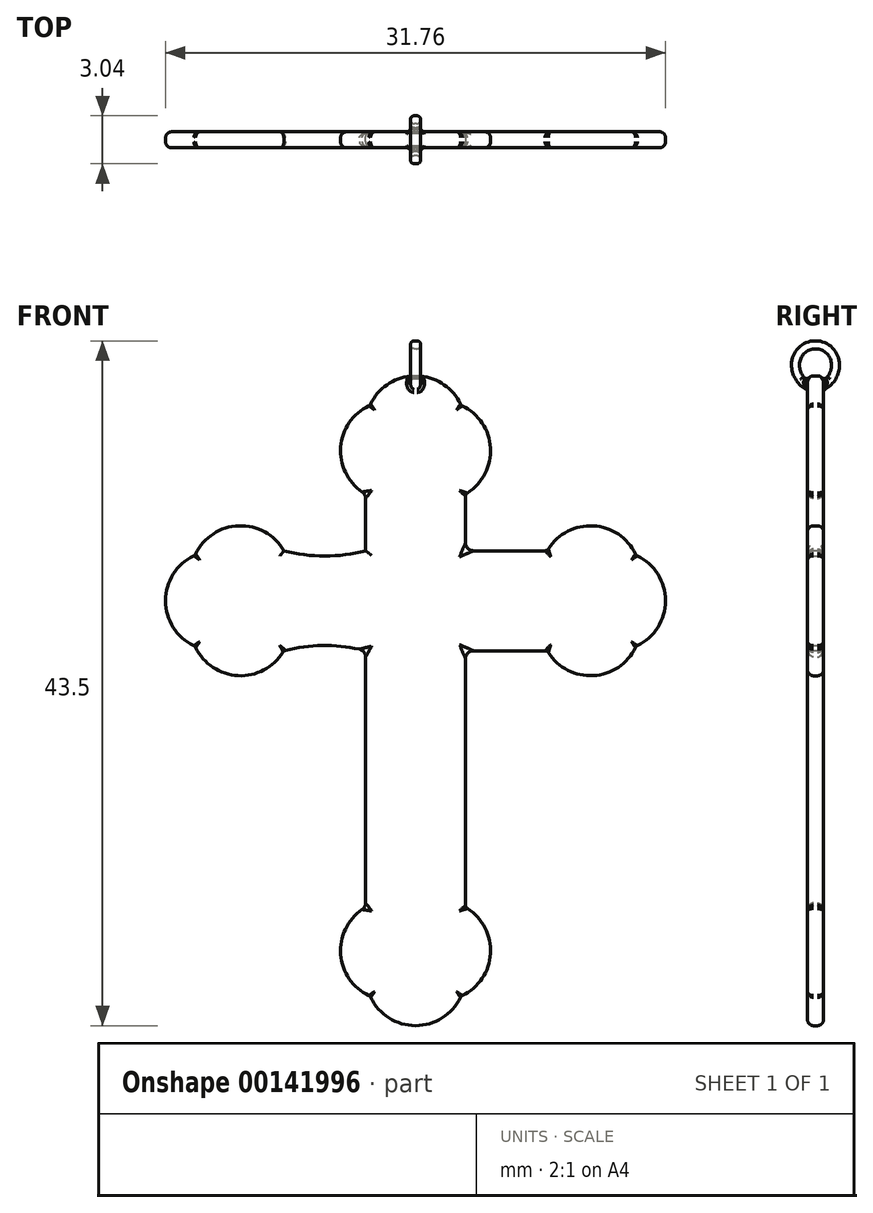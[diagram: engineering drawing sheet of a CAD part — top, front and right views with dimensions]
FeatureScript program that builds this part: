
annotation { "Feature Type Name" : "Feature", "Feature Type Description" : "" }
export const myFeature = defineFeature(function(context is Context, id is Id, definition is map)
    precondition{}
    {
        {
            var Q0;
            Q0=qCreatedBy(makeId("Front.planeOp"),FACE);
            var sketch = newSketch(context, id + "F0", { "sketchPlane" : qUnion([Q0])});
            skLineSegment(sketch, "E0", {"start": v(-3.17, 3.18) * mm, "end": v(-3.17, 6.78) * mm});
            skLineSegment(sketch, "E1", {"start": v(-3.17, 11.11) * mm, "end": v(0, 11.11) * mm, "construction": true});
            skLineSegment(sketch, "E2", {"start": v(0, 11.11) * mm, "end": v(0, -23.81) * mm, "construction": true});
            skLineSegment(sketch, "E3", {"start": v(0, -23.81) * mm, "end": v(-3.17, -23.81) * mm, "construction": true});
            skLineSegment(sketch, "E4", {"start": v(-3.17, -19.48) * mm, "end": v(-3.17, -3.17) * mm});
            skLineSegment(sketch, "E5", {"start": v(-3.17, -3.17) * mm, "end": v(-8.36, -3.17) * mm, "construction": true});
            skLineSegment(sketch, "E6", {"start": v(-12.7, -3.18) * mm, "end": v(-12.7, 0) * mm, "construction": true});
            skLineSegment(sketch, "E7", {"start": v(-8.36, 3.18) * mm, "end": v(-3.17, 3.18) * mm, "construction": true});
            skLineSegment(sketch, "E8", {"start": v(0, 0) * mm, "end": v(-12.7, 0) * mm, "construction": true});
            skLineSegment(sketch, "E9.MirrorCS", {"start": v(3.17, 3.18) * mm, "end": v(3.17, 6.78) * mm});
            skLineSegment(sketch, "E10.MirrorCS", {"start": v(3.17, -19.48) * mm, "end": v(3.17, -3.17) * mm});
            skLineSegment(sketch, "E11.MirrorCS", {"start": v(0, 0) * mm, "end": v(12.7, 0) * mm, "construction": true});
            skLineSegment(sketch, "E12.MirrorCS", {"start": v(12.7, -3.18) * mm, "end": v(12.7, 0) * mm, "construction": true});
            skLineSegment(sketch, "E13.MirrorCS", {"start": v(8.36, 3.18) * mm, "end": v(3.17, 3.18) * mm});
            skLineSegment(sketch, "E14.MirrorCS", {"start": v(3.17, -3.17) * mm, "end": v(8.36, -3.17) * mm});
            skArc(sketch, "E15", {"start": v(2.9, 12.42) * mm, "mid": v(0, 14.29) * mm, "end": v(-2.9, 12.42) * mm});
            skArc(sketch, "E16", {"start": v(-2.9, 12.42) * mm, "mid": v(-4.76, 9.68) * mm, "end": v(-3.17, 6.78) * mm});
            skLineSegment(sketch, "E17", {"start": v(-3.17, 11.11) * mm, "end": v(-1.59, 9.53) * mm, "construction": true});
            skLineSegment(sketch, "E18", {"start": v(0, 11.11) * mm, "end": v(-1.59, 9.53) * mm, "construction": true});
            skArc(sketch, "E19.MirrorCS", {"start": v(2.9, 12.42) * mm, "mid": v(4.76, 9.68) * mm, "end": v(3.17, 6.78) * mm});
            skPoint(sketch, "E20.orphan", {"position": v(3.17, 11.11) * mm});
            skArc(sketch, "E21", {"start": v(-14, 2.9) * mm, "mid": v(-15.88, 0) * mm, "end": v(-14, -2.9) * mm});
            skLineSegment(sketch, "E22", {"start": v(-12.7, -3.18) * mm, "end": v(-11.11, -1.59) * mm, "construction": true});
            skLineSegment(sketch, "E23", {"start": v(-11.11, -1.59) * mm, "end": v(-12.7, 0) * mm, "construction": true});
            skArc(sketch, "E24", {"start": v(-14, -2.9) * mm, "mid": v(-11.27, -4.76) * mm, "end": v(-8.36, -3.17) * mm});
            skArc(sketch, "E25.MirrorCS", {"start": v(-14, 2.9) * mm, "mid": v(-11.27, 4.76) * mm, "end": v(-8.36, 3.17) * mm});
            skPoint(sketch, "E26.orphan", {"position": v(-12.7, 3.17) * mm});
            skArc(sketch, "E27.MirrorCS", {"start": v(14, 2.9) * mm, "mid": v(11.27, 4.76) * mm, "end": v(8.36, 3.17) * mm});
            skArc(sketch, "E28.MirrorCS", {"start": v(14, 2.9) * mm, "mid": v(15.88, 0) * mm, "end": v(14, -2.9) * mm});
            skArc(sketch, "E29.MirrorCS", {"start": v(14, -2.9) * mm, "mid": v(11.27, -4.76) * mm, "end": v(8.36, -3.17) * mm});
            skPoint(sketch, "E30.orphan", {"position": v(12.7, 3.18) * mm});
            skArc(sketch, "E31", {"start": v(-2.9, -25.12) * mm, "mid": v(0, -26.99) * mm, "end": v(2.9, -25.12) * mm});
            skLineSegment(sketch, "E32", {"start": v(-3.17, -23.81) * mm, "end": v(-1.59, -22.23) * mm, "construction": true});
            skLineSegment(sketch, "E33", {"start": v(-1.59, -22.23) * mm, "end": v(0, -23.81) * mm, "construction": true});
            skArc(sketch, "E34", {"start": v(-3.17, -19.48) * mm, "mid": v(-4.76, -22.38) * mm, "end": v(-2.9, -25.12) * mm});
            skArc(sketch, "E35.MirrorCS", {"start": v(3.17, -19.48) * mm, "mid": v(4.76, -22.38) * mm, "end": v(2.9, -25.12) * mm});
            skArc(sketch, "E36", {"start": v(-8.36, 3.18) * mm, "mid": v(-5.77, 2.84) * mm, "end": v(-3.17, 3.18) * mm});
            skArc(sketch, "E37.MirrorCS", {"start": v(-8.36, -3.18) * mm, "mid": v(-5.77, -2.84) * mm, "end": v(-3.17, -3.18) * mm});
            skLineSegment(sketch, "E38.MirrorCS", {"start": v(-3.17, 3.17) * mm, "end": v(-8.36, 3.17) * mm});
            skSolve(sketch);
        }
        {
            var Q0;
            Q0=makeQuery(id+"F0.imprint","IMPRINT",FACE,{"disambiguationData":[TD([[makeQuery(id+"F0.imprint","IMPRINT",EDGE,{"derivedFrom":sQuery(id+"F0.wireOp",EDGE,"E0")}),-1.0]])]});
            extrude(context, id + "F1", {"entities" : qUnion([Q0]), "endBound" : BoundingType.SYMMETRIC, "depth" : 1.02 * mm});
        }
        {
            var Q0;
            Q0=makeQuery(id+"F1.opExtrude","CAP_FACE",FACE,{"disambiguationData":[OSD([sQuery(id+"F0.wireOp",EDGE,"E0"),sQuery(id+"F0.wireOp",EDGE,"E4"),sQuery(id+"F0.wireOp",EDGE,"E5"),sQuery(id+"F0.wireOp",EDGE,"E7"),sQuery(id+"F0.wireOp",EDGE,"E9.MirrorCS"),sQuery(id+"F0.wireOp",EDGE,"E10.MirrorCS"),sQuery(id+"F0.wireOp",EDGE,"E13.MirrorCS"),sQuery(id+"F0.wireOp",EDGE,"E14.MirrorCS"),sQuery(id+"F0.wireOp",EDGE,"E15"),sQuery(id+"F0.wireOp",EDGE,"E16"),sQuery(id+"F0.wireOp",EDGE,"E19.MirrorCS"),sQuery(id+"F0.wireOp",EDGE,"E21"),sQuery(id+"F0.wireOp",EDGE,"E24"),sQuery(id+"F0.wireOp",EDGE,"E25.MirrorCS"),sQuery(id+"F0.wireOp",EDGE,"E27.MirrorCS"),sQuery(id+"F0.wireOp",EDGE,"E28.MirrorCS"),sQuery(id+"F0.wireOp",EDGE,"E29.MirrorCS"),sQuery(id+"F0.wireOp",EDGE,"E31"),sQuery(id+"F0.wireOp",EDGE,"E34"),sQuery(id+"F0.wireOp",EDGE,"E35.MirrorCS")])],"isStart":false});
            fillet(context, id + "F2", {"entities" : qUnion([Q0]), "radius" : 0.38 * mm, "tangentPropagation" : true, "allowEdgeOverflow" : false});
        }
        {
            var Q0;
            Q0=makeQuery(id+"F1.opExtrude","CAP_FACE",FACE,{"disambiguationData":[OSD([sQuery(id+"F0.wireOp",EDGE,"E0"),sQuery(id+"F0.wireOp",EDGE,"E4"),sQuery(id+"F0.wireOp",EDGE,"E5"),sQuery(id+"F0.wireOp",EDGE,"E7"),sQuery(id+"F0.wireOp",EDGE,"E9.MirrorCS"),sQuery(id+"F0.wireOp",EDGE,"E10.MirrorCS"),sQuery(id+"F0.wireOp",EDGE,"E13.MirrorCS"),sQuery(id+"F0.wireOp",EDGE,"E14.MirrorCS"),sQuery(id+"F0.wireOp",EDGE,"E15"),sQuery(id+"F0.wireOp",EDGE,"E16"),sQuery(id+"F0.wireOp",EDGE,"E19.MirrorCS"),sQuery(id+"F0.wireOp",EDGE,"E21"),sQuery(id+"F0.wireOp",EDGE,"E24"),sQuery(id+"F0.wireOp",EDGE,"E25.MirrorCS"),sQuery(id+"F0.wireOp",EDGE,"E27.MirrorCS"),sQuery(id+"F0.wireOp",EDGE,"E28.MirrorCS"),sQuery(id+"F0.wireOp",EDGE,"E29.MirrorCS"),sQuery(id+"F0.wireOp",EDGE,"E31"),sQuery(id+"F0.wireOp",EDGE,"E34"),sQuery(id+"F0.wireOp",EDGE,"E35.MirrorCS")])],"isStart":true});
            fillet(context, id + "F3", {"entities" : qUnion([Q0]), "radius" : 0.38 * mm, "tangentPropagation" : true, "allowEdgeOverflow" : false});
        }
        {
            var Q0;
            Q0=qCreatedBy(makeId("Right.planeOp"),FACE);
            var sketch = newSketch(context, id + "F4", { "sketchPlane" : qUnion([Q0])});
            skLineSegment(sketch, "E39", {"start": v(0, 0) * mm, "end": v(0, 14.99) * mm, "construction": true});
            skArc(sketch, "E40", {"start": v(-1.02, 14.99) * mm, "mid": v(-0.73, 14.18) * mm, "end": v(0, 13.74) * mm});
            skLineSegment(sketch, "E41", {"start": v(0, 14.99) * mm, "end": v(0.25, 14.99) * mm, "construction": true});
            skLineSegment(sketch, "E42", {"start": v(0, 14.99) * mm, "end": v(-0.25, 14.99) * mm, "construction": true});
            skArc(sketch, "E43", {"start": v(0, 13.74) * mm, "mid": v(0.73, 14.18) * mm, "end": v(1.02, 14.99) * mm});
            skArc(sketch, "E44", {"start": v(1.02, 14.99) * mm, "mid": v(0, 16) * mm, "end": v(-1.02, 14.99) * mm});
            skArc(sketch, "E45.0", {"start": v(1.52, 14.99) * mm, "mid": v(0, 16.51) * mm, "end": v(-1.52, 14.99) * mm});
            skArc(sketch, "E46.0", {"start": v(-1.52, 14.99) * mm, "mid": v(-1.1, 13.82) * mm, "end": v(0, 13.23) * mm});
            skArc(sketch, "E47.0", {"start": v(0, 13.23) * mm, "mid": v(1.1, 13.82) * mm, "end": v(1.52, 14.99) * mm});
            skSolve(sketch);
        }
        {
            var Q0;
            Q0=qSketchRegion(id+"F4",true);
            extrude(context, id + "F5", {"entities" : qUnion([Q0]), "operationType" : NewBodyOperationType.ADD, "endBound" : BoundingType.SYMMETRIC, "depth" : 0.64 * mm});
        }
        {
            var Q0;
            Q0=makeQuery(id+"F5.opExtrude","SWEPT_FACE",FACE,{"disambiguationData":[OSD([sQuery(id+"F4.wireOp",EDGE,"E45.0")])]});
            fillet(context, id + "F6", {"entities" : qUnion([Q0]), "radius" : 0.23 * mm, "tangentPropagation" : true, "allowEdgeOverflow" : false});
        }
        {
            var Q0;
            Q0=makeQuery(id+"F6.opFillet","BLEND_EDGE",EDGE,{"blendedFrom":[makeQuery(id+"F5.opExtrude","CAP_EDGE",EDGE,{"disambiguationData":[OSD([sQuery(id+"F4.wireOp",EDGE,"E47.0")])],"isStart":false}),makeQuery(id+"F1.opExtrude","CAP_FACE",FACE,{"disambiguationData":[OSD([sQuery(id+"F0.wireOp",EDGE,"E0"),sQuery(id+"F0.wireOp",EDGE,"E4"),sQuery(id+"F0.wireOp",EDGE,"E5"),sQuery(id+"F0.wireOp",EDGE,"E7"),sQuery(id+"F0.wireOp",EDGE,"E9.MirrorCS"),sQuery(id+"F0.wireOp",EDGE,"E10.MirrorCS"),sQuery(id+"F0.wireOp",EDGE,"E13.MirrorCS"),sQuery(id+"F0.wireOp",EDGE,"E14.MirrorCS"),sQuery(id+"F0.wireOp",EDGE,"E15"),sQuery(id+"F0.wireOp",EDGE,"E16"),sQuery(id+"F0.wireOp",EDGE,"E19.MirrorCS"),sQuery(id+"F0.wireOp",EDGE,"E21"),sQuery(id+"F0.wireOp",EDGE,"E24"),sQuery(id+"F0.wireOp",EDGE,"E25.MirrorCS"),sQuery(id+"F0.wireOp",EDGE,"E27.MirrorCS"),sQuery(id+"F0.wireOp",EDGE,"E28.MirrorCS"),sQuery(id+"F0.wireOp",EDGE,"E29.MirrorCS"),sQuery(id+"F0.wireOp",EDGE,"E31"),sQuery(id+"F0.wireOp",EDGE,"E34"),sQuery(id+"F0.wireOp",EDGE,"E35.MirrorCS")])],"isStart":true})],"blendedInto":[makeQuery(id+"F1.opExtrude","CAP_FACE",FACE,{"disambiguationData":[OSD([sQuery(id+"F0.wireOp",EDGE,"E0"),sQuery(id+"F0.wireOp",EDGE,"E4"),sQuery(id+"F0.wireOp",EDGE,"E5"),sQuery(id+"F0.wireOp",EDGE,"E7"),sQuery(id+"F0.wireOp",EDGE,"E9.MirrorCS"),sQuery(id+"F0.wireOp",EDGE,"E10.MirrorCS"),sQuery(id+"F0.wireOp",EDGE,"E13.MirrorCS"),sQuery(id+"F0.wireOp",EDGE,"E14.MirrorCS"),sQuery(id+"F0.wireOp",EDGE,"E15"),sQuery(id+"F0.wireOp",EDGE,"E16"),sQuery(id+"F0.wireOp",EDGE,"E19.MirrorCS"),sQuery(id+"F0.wireOp",EDGE,"E21"),sQuery(id+"F0.wireOp",EDGE,"E24"),sQuery(id+"F0.wireOp",EDGE,"E25.MirrorCS"),sQuery(id+"F0.wireOp",EDGE,"E27.MirrorCS"),sQuery(id+"F0.wireOp",EDGE,"E28.MirrorCS"),sQuery(id+"F0.wireOp",EDGE,"E29.MirrorCS"),sQuery(id+"F0.wireOp",EDGE,"E31"),sQuery(id+"F0.wireOp",EDGE,"E34"),sQuery(id+"F0.wireOp",EDGE,"E35.MirrorCS")])],"isStart":true})]});
            fillet(context, id + "F7", {"entities" : qUnion([Q0]), "radius" : 0.25 * mm, "tangentPropagation" : true, "allowEdgeOverflow" : false});
        }
        {
            var Q0;
            Q0=makeQuery(id+"F6.opFillet","BLEND_EDGE",EDGE,{"blendedFrom":[makeQuery(id+"F5.opExtrude","CAP_EDGE",EDGE,{"disambiguationData":[OSD([sQuery(id+"F4.wireOp",EDGE,"E46.0")])],"isStart":true}),makeQuery(id+"F1.opExtrude","CAP_FACE",FACE,{"disambiguationData":[OSD([sQuery(id+"F0.wireOp",EDGE,"E0"),sQuery(id+"F0.wireOp",EDGE,"E4"),sQuery(id+"F0.wireOp",EDGE,"E5"),sQuery(id+"F0.wireOp",EDGE,"E7"),sQuery(id+"F0.wireOp",EDGE,"E9.MirrorCS"),sQuery(id+"F0.wireOp",EDGE,"E10.MirrorCS"),sQuery(id+"F0.wireOp",EDGE,"E13.MirrorCS"),sQuery(id+"F0.wireOp",EDGE,"E14.MirrorCS"),sQuery(id+"F0.wireOp",EDGE,"E15"),sQuery(id+"F0.wireOp",EDGE,"E16"),sQuery(id+"F0.wireOp",EDGE,"E19.MirrorCS"),sQuery(id+"F0.wireOp",EDGE,"E21"),sQuery(id+"F0.wireOp",EDGE,"E24"),sQuery(id+"F0.wireOp",EDGE,"E25.MirrorCS"),sQuery(id+"F0.wireOp",EDGE,"E27.MirrorCS"),sQuery(id+"F0.wireOp",EDGE,"E28.MirrorCS"),sQuery(id+"F0.wireOp",EDGE,"E29.MirrorCS"),sQuery(id+"F0.wireOp",EDGE,"E31"),sQuery(id+"F0.wireOp",EDGE,"E34"),sQuery(id+"F0.wireOp",EDGE,"E35.MirrorCS")])],"isStart":false})],"blendedInto":[makeQuery(id+"F1.opExtrude","CAP_FACE",FACE,{"disambiguationData":[OSD([sQuery(id+"F0.wireOp",EDGE,"E0"),sQuery(id+"F0.wireOp",EDGE,"E4"),sQuery(id+"F0.wireOp",EDGE,"E5"),sQuery(id+"F0.wireOp",EDGE,"E7"),sQuery(id+"F0.wireOp",EDGE,"E9.MirrorCS"),sQuery(id+"F0.wireOp",EDGE,"E10.MirrorCS"),sQuery(id+"F0.wireOp",EDGE,"E13.MirrorCS"),sQuery(id+"F0.wireOp",EDGE,"E14.MirrorCS"),sQuery(id+"F0.wireOp",EDGE,"E15"),sQuery(id+"F0.wireOp",EDGE,"E16"),sQuery(id+"F0.wireOp",EDGE,"E19.MirrorCS"),sQuery(id+"F0.wireOp",EDGE,"E21"),sQuery(id+"F0.wireOp",EDGE,"E24"),sQuery(id+"F0.wireOp",EDGE,"E25.MirrorCS"),sQuery(id+"F0.wireOp",EDGE,"E27.MirrorCS"),sQuery(id+"F0.wireOp",EDGE,"E28.MirrorCS"),sQuery(id+"F0.wireOp",EDGE,"E29.MirrorCS"),sQuery(id+"F0.wireOp",EDGE,"E31"),sQuery(id+"F0.wireOp",EDGE,"E34"),sQuery(id+"F0.wireOp",EDGE,"E35.MirrorCS")])],"isStart":false})]});
            fillet(context, id + "F8", {"entities" : qUnion([Q0]), "radius" : 0.25 * mm, "tangentPropagation" : true, "allowEdgeOverflow" : false});
        }
        {
            var Q0;
            Q0=makeQuery(id+"F5.boolean.opBoolean","INTERSECT",EDGE,{"derivedFrom":[makeQuery(id+"F2.opFillet","BLEND_FACE",FACE,{"disambiguationData":[OSD([sQuery(id+"F0.wireOp",EDGE,"E15")])]}),makeQuery(id+"F5.opExtrude","SWEPT_FACE",FACE,{"disambiguationData":[OSD([sQuery(id+"F4.wireOp",EDGE,"E40")])]})]});
            var Q1;
            Q1=makeQuery(id+"F5.boolean.opBoolean","INTERSECT",EDGE,{"derivedFrom":[makeQuery(id+"F3.opFillet","BLEND_FACE",FACE,{"disambiguationData":[OSD([sQuery(id+"F0.wireOp",EDGE,"E15")])]}),makeQuery(id+"F5.opExtrude","SWEPT_FACE",FACE,{"disambiguationData":[OSD([sQuery(id+"F4.wireOp",EDGE,"E43")])]})]});
            fillet(context, id + "F9", {"entities" : qUnion([Q0, Q1]), "radius" : 0.25 * mm, "tangentPropagation" : true, "allowEdgeOverflow" : false});
        }
        {
            var Q0;
            Q0=makeQuery(id+"F5.opExtrude","SWEPT_FACE",FACE,{"disambiguationData":[OSD([sQuery(id+"F4.wireOp",EDGE,"E40")])]});
            fillet(context, id + "F10", {"entities" : qUnion([Q0]), "radius" : 0.25 * mm, "tangentPropagation" : true, "allowEdgeOverflow" : false});
        }
        {
            var Q0;
            Q0=makeQuery(id+"F1.opExtrude","SWEPT_EDGE",EDGE,{"disambiguationData":[OSD([sQuery(id+"F0.wireOp",EDGE,"E9.MirrorCS"),sQuery(id+"F0.wireOp",EDGE,"E13.MirrorCS")])]});
            var Q1;
            Q1=makeQuery(id+"F1.opExtrude","SWEPT_EDGE",EDGE,{"disambiguationData":[OSD([sQuery(id+"F0.wireOp",EDGE,"E10.MirrorCS"),sQuery(id+"F0.wireOp",EDGE,"E14.MirrorCS")])]});
            var Q2;
            Q2=makeQuery(id+"F1.opExtrude","SWEPT_EDGE",EDGE,{"disambiguationData":[OSD([sQuery(id+"F0.wireOp",EDGE,"E4"),sQuery(id+"F0.wireOp",EDGE,"E5")])]});
            var Q3;
            Q3=makeQuery(id+"F1.opExtrude","SWEPT_EDGE",EDGE,{"disambiguationData":[OSD([sQuery(id+"F0.wireOp",EDGE,"E0"),sQuery(id+"F0.wireOp",EDGE,"E7")])]});
            fillet(context, id + "F11", {"entities" : qUnion([Q0, Q1, Q2, Q3]), "radius" : 0.5 * mm, "tangentPropagation" : true, "allowEdgeOverflow" : false});
        }
        {
            var Q0;
            Q0=makeQuery(id+"F1.opExtrude","SWEPT_EDGE",EDGE,{"disambiguationData":[OSD([sQuery(id+"F0.wireOp",EDGE,"E0"),sQuery(id+"F0.wireOp",EDGE,"E16")])]});
            var Q1;
            Q1=makeQuery(id+"F1.opExtrude","SWEPT_EDGE",EDGE,{"disambiguationData":[OSD([sQuery(id+"F0.wireOp",EDGE,"E9.MirrorCS"),sQuery(id+"F0.wireOp",EDGE,"E19.MirrorCS")])]});
            var Q2;
            Q2=makeQuery(id+"F1.opExtrude","SWEPT_EDGE",EDGE,{"disambiguationData":[OSD([sQuery(id+"F0.wireOp",EDGE,"E13.MirrorCS"),sQuery(id+"F0.wireOp",EDGE,"E27.MirrorCS")])]});
            var Q3;
            Q3=makeQuery(id+"F1.opExtrude","SWEPT_EDGE",EDGE,{"disambiguationData":[OSD([sQuery(id+"F0.wireOp",EDGE,"E7"),sQuery(id+"F0.wireOp",EDGE,"E25.MirrorCS")])]});
            var Q4;
            Q4=makeQuery(id+"F1.opExtrude","SWEPT_EDGE",EDGE,{"disambiguationData":[OSD([sQuery(id+"F0.wireOp",EDGE,"E5"),sQuery(id+"F0.wireOp",EDGE,"E24")])]});
            var Q5;
            Q5=makeQuery(id+"F1.opExtrude","SWEPT_EDGE",EDGE,{"disambiguationData":[OSD([sQuery(id+"F0.wireOp",EDGE,"E14.MirrorCS"),sQuery(id+"F0.wireOp",EDGE,"E29.MirrorCS")])]});
            var Q6;
            Q6=makeQuery(id+"F1.opExtrude","SWEPT_EDGE",EDGE,{"disambiguationData":[OSD([sQuery(id+"F0.wireOp",EDGE,"E10.MirrorCS"),sQuery(id+"F0.wireOp",EDGE,"E35.MirrorCS")])]});
            var Q7;
            Q7=makeQuery(id+"F1.opExtrude","SWEPT_EDGE",EDGE,{"disambiguationData":[OSD([sQuery(id+"F0.wireOp",EDGE,"E4"),sQuery(id+"F0.wireOp",EDGE,"E34")])]});
            var Q8;
            Q8=makeQuery(id+"F1.opExtrude","SWEPT_EDGE",EDGE,{"disambiguationData":[OSD([sQuery(id+"F0.wireOp",EDGE,"E31"),sQuery(id+"F0.wireOp",EDGE,"E34")])]});
            var Q9;
            Q9=makeQuery(id+"F1.opExtrude","SWEPT_EDGE",EDGE,{"disambiguationData":[OSD([sQuery(id+"F0.wireOp",EDGE,"E31"),sQuery(id+"F0.wireOp",EDGE,"E35.MirrorCS")])]});
            var Q10;
            Q10=makeQuery(id+"F1.opExtrude","SWEPT_EDGE",EDGE,{"disambiguationData":[OSD([sQuery(id+"F0.wireOp",EDGE,"E27.MirrorCS"),sQuery(id+"F0.wireOp",EDGE,"E28.MirrorCS")])]});
            var Q11;
            Q11=makeQuery(id+"F1.opExtrude","SWEPT_EDGE",EDGE,{"disambiguationData":[OSD([sQuery(id+"F0.wireOp",EDGE,"E28.MirrorCS"),sQuery(id+"F0.wireOp",EDGE,"E29.MirrorCS")])]});
            var Q12;
            Q12=makeQuery(id+"F1.opExtrude","SWEPT_EDGE",EDGE,{"disambiguationData":[OSD([sQuery(id+"F0.wireOp",EDGE,"E21"),sQuery(id+"F0.wireOp",EDGE,"E25.MirrorCS")])]});
            var Q13;
            Q13=makeQuery(id+"F1.opExtrude","SWEPT_EDGE",EDGE,{"disambiguationData":[OSD([sQuery(id+"F0.wireOp",EDGE,"E21"),sQuery(id+"F0.wireOp",EDGE,"E24")])]});
            var Q14;
            Q14=makeQuery(id+"F1.opExtrude","SWEPT_EDGE",EDGE,{"disambiguationData":[OSD([sQuery(id+"F0.wireOp",EDGE,"E15"),sQuery(id+"F0.wireOp",EDGE,"E16")])]});
            var Q15;
            Q15=makeQuery(id+"F1.opExtrude","SWEPT_EDGE",EDGE,{"disambiguationData":[OSD([sQuery(id+"F0.wireOp",EDGE,"E15"),sQuery(id+"F0.wireOp",EDGE,"E19.MirrorCS")])]});
            fillet(context, id + "F12", {"entities" : qUnion([Q0, Q1, Q2, Q3, Q4, Q5, Q6, Q7, Q8, Q9, Q10, Q11, Q12, Q13, Q14, Q15]), "radius" : 0.25 * mm, "tangentPropagation" : true, "allowEdgeOverflow" : false});
        }
    });
